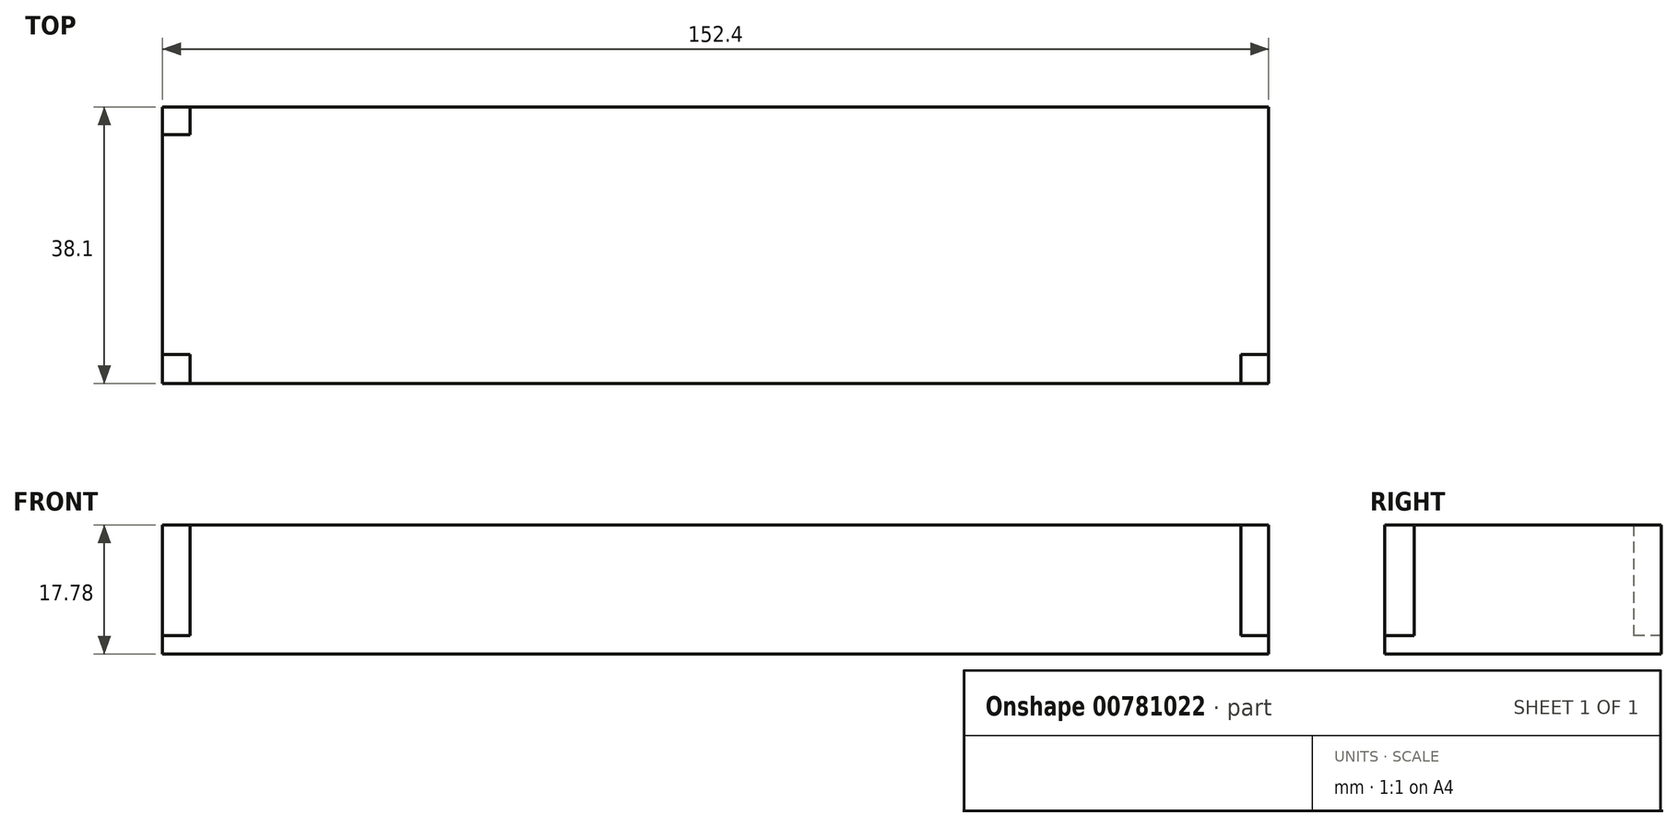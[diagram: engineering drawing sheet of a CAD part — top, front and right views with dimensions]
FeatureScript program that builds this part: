
annotation { "Feature Type Name" : "Feature", "Feature Type Description" : "" }
export const myFeature = defineFeature(function(context is Context, id is Id, definition is map)
    precondition{}
    {
        {
            var Q0;
            Q0=qCreatedBy(makeId("Top.planeOp"),FACE);
            var sketch = newSketch(context, id + "F0", { "sketchPlane" : qUnion([Q0])});
            skLineSegment(sketch, "E0.bottom", {"start": v(76.2, -19.05) * mm, "end": v(-76.2, -19.05) * mm});
            skLineSegment(sketch, "E0.top", {"start": v(76.2, 19.05) * mm, "end": v(-76.2, 19.05) * mm});
            skLineSegment(sketch, "E0.left", {"start": v(76.2, -19.05) * mm, "end": v(76.2, 19.05) * mm});
            skLineSegment(sketch, "E0.right", {"start": v(-76.2, -19.05) * mm, "end": v(-76.2, 19.05) * mm});
            skPoint(sketch, "E0.middle", {"position": v(0, 0) * mm});
            skLineSegment(sketch, "E1.top", {"start": v(-76.2, 19.05) * mm, "end": v(-68.58, 19.05) * mm});
            skLineSegment(sketch, "E2.bottom", {"start": v(-76.2, 19.05) * mm, "end": v(76.2, 19.05) * mm});
            skLineSegment(sketch, "E2.top", {"start": v(-76.2, 15.24) * mm, "end": v(76.2, 15.24) * mm});
            skLineSegment(sketch, "E2.left", {"start": v(-76.2, 19.05) * mm, "end": v(-76.2, 15.24) * mm});
            skLineSegment(sketch, "E2.right", {"start": v(76.2, 19.05) * mm, "end": v(76.2, 15.24) * mm});
            skLineSegment(sketch, "E3.top", {"start": v(72.4, 19.05) * mm, "end": v(76.2, 19.05) * mm});
            skLineSegment(sketch, "E3.left", {"start": v(72.4, -19.05) * mm, "end": v(72.4, 19.05) * mm});
            skLineSegment(sketch, "E4.bottom", {"start": v(-76.2, -19.05) * mm, "end": v(-71.38, -19.05) * mm});
            skLineSegment(sketch, "E4.top", {"start": v(-76.2, 19.05) * mm, "end": v(-72.4, 19.05) * mm});
            skLineSegment(sketch, "E5.left", {"start": v(-76.2, -19.05) * mm, "end": v(-76.2, -15.03) * mm});
            skLineSegment(sketch, "E5.right", {"start": v(76.2, -18.84) * mm, "end": v(76.2, -15.03) * mm});
            skLineSegment(sketch, "E6.bottom", {"start": v(-72.4, 19.05) * mm, "end": v(-76.2, 19.05) * mm});
            skLineSegment(sketch, "E6.top", {"start": v(-72.4, -19.05) * mm, "end": v(-76.2, -19.05) * mm});
            skLineSegment(sketch, "E6.left", {"start": v(-72.4, 19.05) * mm, "end": v(-72.4, -19.05) * mm});
            skLineSegment(sketch, "E6.right", {"start": v(-76.2, 19.05) * mm, "end": v(-76.2, -19.05) * mm});
            skLineSegment(sketch, "E7.bottom", {"start": v(-76.2, -19.05) * mm, "end": v(76.2, -19.05) * mm});
            skLineSegment(sketch, "E7.top", {"start": v(-76.2, -15.03) * mm, "end": v(76.2, -15.03) * mm});
            skLineSegment(sketch, "E7.right", {"start": v(76.2, -19.05) * mm, "end": v(76.2, -15.03) * mm});
            skSolve(sketch);
        }
        {
            var Q0;
            {var subQ0=sQuery(id+"F0.wireOp",EDGE,"E6.left");var subQ5=sQuery(id+"F0.wireOp",EDGE,"E2.top");var subQ6=makeQuery(id+"F0.imprint","INTERSECT",VERTEX,{"derivedFrom":[subQ5,subQ0]});Q0=makeQuery(id+"F0.imprint","IMPRINT",FACE,{"disambiguationData":[TD([[makeQuery(id+"F0.imprint","IMPRINT",EDGE,{"disambiguationData":[TD([[subQ6,-1.0]])],"derivedFrom":subQ5}),1.0]])]});}
            var Q1;
            {var subQ5=sQuery(id+"F0.wireOp",EDGE,"E6.bottom");Q1=makeQuery(id+"F0.imprint","IMPRINT",FACE,{"disambiguationData":[TD([[makeQuery(id+"F0.imprint","IMPRINT",EDGE,{"derivedFrom":subQ5}),1.0]])]});}
            var Q2;
            {var subQ0=sQuery(id+"F0.wireOp",EDGE,"E6.right");var subQ1=sQuery(id+"F0.wireOp",EDGE,"E2.top");var subQ2=makeQuery(id+"F0.imprint","INTERSECT",VERTEX,{"derivedFrom":[subQ1,subQ0]});Q2=makeQuery(id+"F0.imprint","IMPRINT",FACE,{"disambiguationData":[TD([[makeQuery(id+"F0.imprint","IMPRINT",EDGE,{"disambiguationData":[TD([[subQ2,-1.0]])],"derivedFrom":subQ1}),-1.0]])]});}
            var Q3;
            {var subQ5=sQuery(id+"F0.wireOp",EDGE,"E5.left");Q3=makeQuery(id+"F0.imprint","IMPRINT",FACE,{"disambiguationData":[TD([[makeQuery(id+"F0.imprint","IMPRINT",EDGE,{"derivedFrom":subQ5}),-1.0]])]});}
            var Q4;
            {var subQ0=sQuery(id+"F0.wireOp",EDGE,"E7.bottom");var subQ1=sQuery(id+"F0.wireOp",EDGE,"E3.left");var subQ2=makeQuery(id+"F0.imprint","INTERSECT",VERTEX,{"derivedFrom":[subQ1,subQ0]});Q4=makeQuery(id+"F0.imprint","IMPRINT",FACE,{"disambiguationData":[TD([[makeQuery(id+"F0.imprint","IMPRINT",EDGE,{"disambiguationData":[TD([[subQ2,-1.0]])],"derivedFrom":subQ1}),1.0]])]});}
            var Q5;
            {var subQ0=sQuery(id+"F0.wireOp",EDGE,"E0.left");var subQ1=sQuery(id+"F0.wireOp",EDGE,"E2.top");var subQ2=makeQuery(id+"F0.imprint","INTERSECT",VERTEX,{"derivedFrom":[subQ1,subQ0]});Q5=makeQuery(id+"F0.imprint","IMPRINT",FACE,{"disambiguationData":[TD([[makeQuery(id+"F0.imprint","IMPRINT",EDGE,{"disambiguationData":[TD([[subQ2,1.0]])],"derivedFrom":subQ1}),-1.0]])]});}
            var Q6;
            {var subQ0=sQuery(id+"F0.wireOp",EDGE,"E7.bottom");var subQ1=sQuery(id+"F0.wireOp",EDGE,"E3.left");var subQ2=makeQuery(id+"F0.imprint","INTERSECT",VERTEX,{"derivedFrom":[subQ1,subQ0]});Q6=makeQuery(id+"F0.imprint","IMPRINT",FACE,{"disambiguationData":[TD([[makeQuery(id+"F0.imprint","IMPRINT",EDGE,{"disambiguationData":[TD([[subQ2,-1.0]])],"derivedFrom":subQ1}),-1.0]])]});}
            var Q7;
            {var subQ5=sQuery(id+"F0.wireOp",EDGE,"E3.top");Q7=makeQuery(id+"F0.imprint","IMPRINT",FACE,{"disambiguationData":[TD([[makeQuery(id+"F0.imprint","IMPRINT",EDGE,{"derivedFrom":subQ5}),-1.0]])]});}
            extrude(context, id + "F1", {"entities" : qUnion([Q0, Q1, Q2, Q3, Q4, Q5, Q6, Q7]), "depth" : 17.78 * mm, "offsetDistance" : 25.4 * mm});
        }
        {
            var Q0;
            Q0=qCreatedBy(makeId("Top.planeOp"),FACE);
            var sketch = newSketch(context, id + "F2", { "sketchPlane" : qUnion([Q0])});
            skLineSegment(sketch, "E8.bottom", {"start": v(76.2, -19.05) * mm, "end": v(-76.2, -19.05) * mm});
            skLineSegment(sketch, "E8.top", {"start": v(76.2, 19.05) * mm, "end": v(-76.2, 19.05) * mm});
            skLineSegment(sketch, "E8.left", {"start": v(76.2, -19.05) * mm, "end": v(76.2, 19.05) * mm});
            skLineSegment(sketch, "E8.right", {"start": v(-76.2, -19.05) * mm, "end": v(-76.2, 19.05) * mm});
            skPoint(sketch, "E8.middle", {"position": v(0, 0) * mm});
            skSolve(sketch);
        }
        {
            var Q0;
            Q0 = qSketchRegion(id + "F2", true);
            extrude(context, id + "F3", {"entities" : qUnion([Q0]), "operationType" : NewBodyOperationType.ADD, "depth" : 2.54 * mm, "offsetDistance" : 25.4 * mm});
        }
    });
